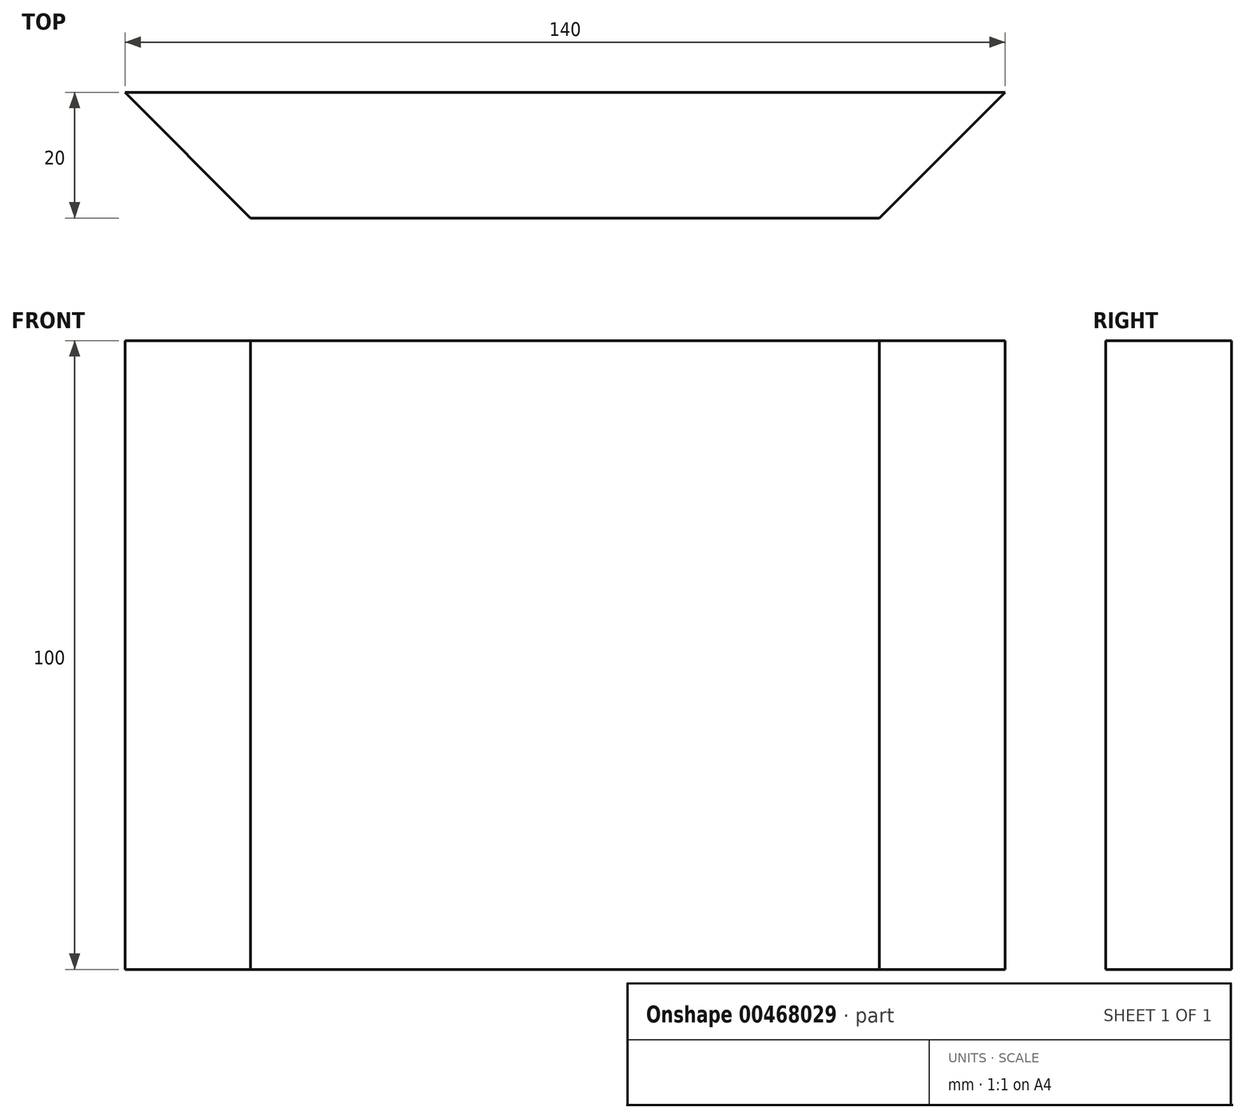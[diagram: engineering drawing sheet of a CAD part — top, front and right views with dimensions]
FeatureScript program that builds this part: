
annotation { "Feature Type Name" : "Feature", "Feature Type Description" : "" }
export const myFeature = defineFeature(function(context is Context, id is Id, definition is map)
    precondition{}
    {
        {
            var Q0;
            Q0=qCreatedBy(makeId("Front.planeOp"),FACE);
            var sketch = newSketch(context, id + "F0", { "sketchPlane" : qUnion([Q0])});
            skLineSegment(sketch, "E0.bottom", {"start": v(0, 0) * mm, "end": v(140, 0) * mm});
            skLineSegment(sketch, "E0.top", {"start": v(0, 100) * mm, "end": v(140, 100) * mm});
            skLineSegment(sketch, "E0.left", {"start": v(0, 0) * mm, "end": v(0, 100) * mm});
            skLineSegment(sketch, "E0.right", {"start": v(140, 0) * mm, "end": v(140, 100) * mm});
            skSolve(sketch);
        }
        {
            var Q0;
            Q0=makeQuery(id+"F0.imprint","IMPRINT",FACE,{"disambiguationData":[TD([[makeQuery(id+"F0.imprint","IMPRINT",EDGE,{"derivedFrom":sQuery(id+"F0.wireOp",EDGE,"E0.bottom")}),1.0]])]});
            extrude(context, id + "F1", {"entities" : qUnion([Q0]), "endBound" : BoundingType.SYMMETRIC, "depth" : 20 * mm});
        }
        {
            var Q0;
            Q0=makeQuery(id+"F1.opExtrude","CAP_EDGE",EDGE,{"disambiguationData":[OSD([sQuery(id+"F0.wireOp",EDGE,"E0.right")])],"isStart":false});
            chamfer(context, id + "F2", {"entities" : qUnion([Q0]), "chamferType" : ChamferType.OFFSET_ANGLE, "width" : 20 * mm, "oppositeDirection" : false, "angle" : 45 * degree, "tangentPropagation" : true});
        }
        {
            var Q0;
            Q0=makeQuery(id+"F1.opExtrude","CAP_EDGE",EDGE,{"disambiguationData":[OSD([sQuery(id+"F0.wireOp",EDGE,"E0.left")])],"isStart":false});
            chamfer(context, id + "F3", {"entities" : qUnion([Q0]), "chamferType" : ChamferType.OFFSET_ANGLE, "width" : 20 * mm, "oppositeDirection" : false, "angle" : 45 * degree, "tangentPropagation" : true});
        }
    });
